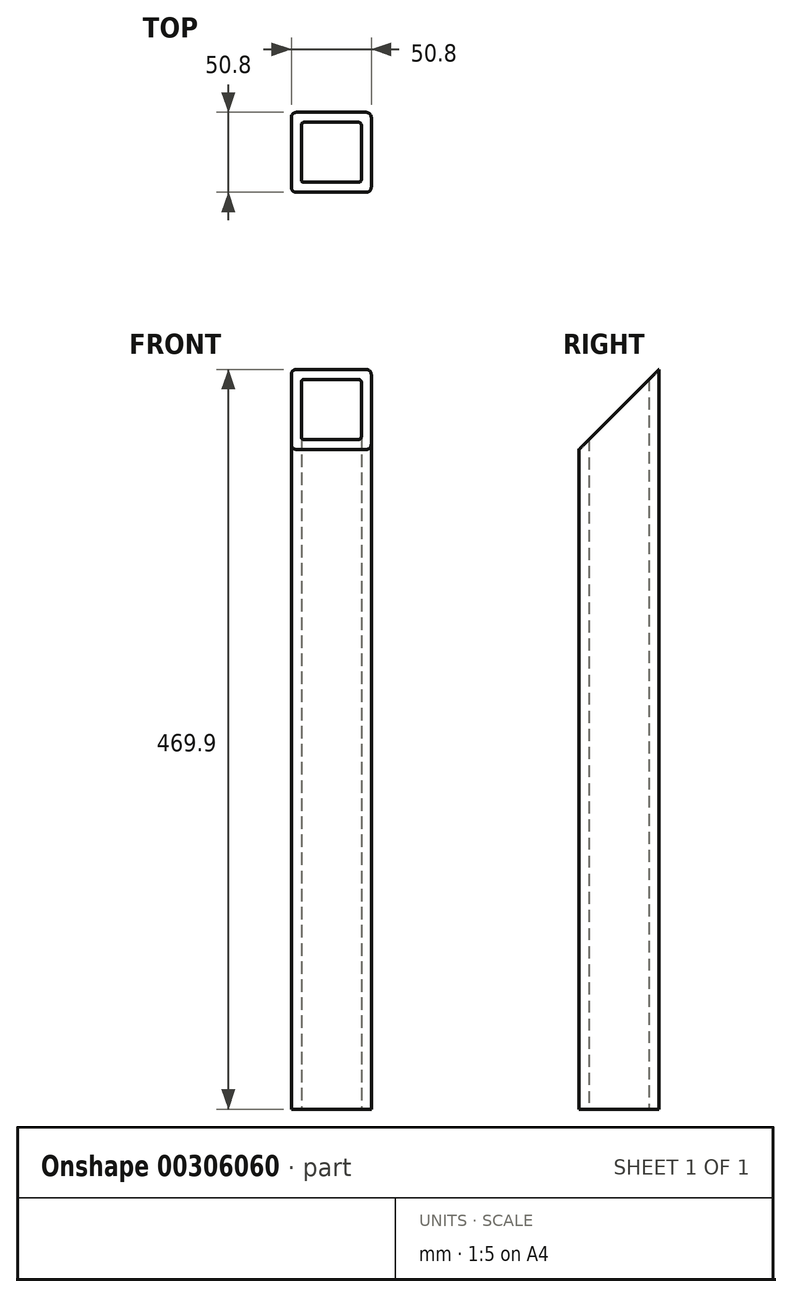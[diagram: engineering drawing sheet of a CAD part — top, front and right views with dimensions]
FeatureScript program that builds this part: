
annotation { "Feature Type Name" : "Feature", "Feature Type Description" : "" }
export const myFeature = defineFeature(function(context is Context, id is Id, definition is map)
    precondition{}
    {
        {
            var Q0;
            Q0=qCreatedBy(makeId("Top.planeOp"),FACE);
            var sketch = newSketch(context, id + "F0", { "sketchPlane" : qUnion([Q0])});
            skLineSegment(sketch, "E0.bottom", {"start": v(-22.22, 25.4) * mm, "end": v(22.23, 25.4) * mm});
            skLineSegment(sketch, "E0.top", {"start": v(-22.23, -25.4) * mm, "end": v(22.23, -25.4) * mm});
            skLineSegment(sketch, "E0.left", {"start": v(-25.4, 22.22) * mm, "end": v(-25.4, -22.23) * mm});
            skLineSegment(sketch, "E0.right", {"start": v(25.4, 22.22) * mm, "end": v(25.4, -22.23) * mm});
            skPoint(sketch, "E0.middle", {"position": v(0, 0) * mm});
            skPoint(sketch, "E1.visualSharp", {"position": v(-25.4, 25.4) * mm});
            skArc(sketch, "E1.filletArc", {"start": v(-22.22, 25.4) * mm, "mid": v(-24.47, 24.47) * mm, "end": v(-25.4, 22.22) * mm});
            skPoint(sketch, "E2.visualSharp", {"position": v(-25.4, -25.4) * mm});
            skArc(sketch, "E2.filletArc", {"start": v(-25.4, -22.23) * mm, "mid": v(-24.47, -24.47) * mm, "end": v(-22.23, -25.4) * mm});
            skPoint(sketch, "E3.visualSharp", {"position": v(25.4, -25.4) * mm});
            skArc(sketch, "E3.filletArc", {"start": v(22.23, -25.4) * mm, "mid": v(24.47, -24.47) * mm, "end": v(25.4, -22.23) * mm});
            skPoint(sketch, "E4.visualSharp", {"position": v(25.4, 25.4) * mm});
            skArc(sketch, "E4.filletArc", {"start": v(25.4, 22.22) * mm, "mid": v(24.47, 24.47) * mm, "end": v(22.23, 25.4) * mm});
            skLineSegment(sketch, "E5.0", {"start": v(-17.46, 19.05) * mm, "end": v(17.46, 19.05) * mm});
            skLineSegment(sketch, "E5.1", {"start": v(-19.05, 17.46) * mm, "end": v(-19.05, -17.46) * mm});
            skLineSegment(sketch, "E5.2", {"start": v(-17.46, -19.05) * mm, "end": v(17.46, -19.05) * mm});
            skLineSegment(sketch, "E5.3", {"start": v(19.05, 17.46) * mm, "end": v(19.05, -17.46) * mm});
            skPoint(sketch, "E6.visualSharp", {"position": v(-19.05, 19.05) * mm});
            skArc(sketch, "E6.filletArc", {"start": v(-17.46, 19.05) * mm, "mid": v(-18.59, 18.59) * mm, "end": v(-19.05, 17.46) * mm});
            skPoint(sketch, "E7.visualSharp", {"position": v(-19.05, -19.05) * mm});
            skArc(sketch, "E7.filletArc", {"start": v(-19.05, -17.46) * mm, "mid": v(-18.59, -18.59) * mm, "end": v(-17.46, -19.05) * mm});
            skPoint(sketch, "E8.visualSharp", {"position": v(19.05, -19.05) * mm});
            skArc(sketch, "E8.filletArc", {"start": v(17.46, -19.05) * mm, "mid": v(18.59, -18.59) * mm, "end": v(19.05, -17.46) * mm});
            skPoint(sketch, "E9.visualSharp", {"position": v(19.05, 19.05) * mm});
            skArc(sketch, "E9.filletArc", {"start": v(19.05, 17.46) * mm, "mid": v(18.59, 18.59) * mm, "end": v(17.46, 19.05) * mm});
            skSolve(sketch);
        }
        {
            var Q0;
            Q0=makeQuery(id+"F0.imprint","IMPRINT",FACE,{"disambiguationData":[TD([[makeQuery(id+"F0.imprint","IMPRINT",EDGE,{"derivedFrom":sQuery(id+"F0.wireOp",EDGE,"E0.bottom")}),-1.0]])]});
            extrude(context, id + "F1", {"entities" : qUnion([Q0]), "depth" : 469.9 * mm});
        }
        {
            var Q0;
            Q0=makeQuery(id+"F1.opExtrude","SWEPT_FACE",FACE,{"disambiguationData":[OSD([sQuery(id+"F0.wireOp",EDGE,"E0.right")])]});
            var sketch = newSketch(context, id + "F2", { "sketchPlane" : qUnion([Q0])});
            skLineSegment(sketch, "E10", {"start": v(25.4, 469.9) * mm, "end": v(-25.4, 419.1) * mm});
            skLineSegment(sketch, "E11", {"start": v(-25.4, 419.1) * mm, "end": v(-25.4, 469.9) * mm});
            skLineSegment(sketch, "E12", {"start": v(-25.4, 469.9) * mm, "end": v(25.4, 469.9) * mm});
            skSolve(sketch);
        }
        {
            var Q0;
            Q0=qSketchRegion(id+"F2",true);
            extrude(context, id + "F3", {"entities" : qUnion([Q0]), "operationType" : NewBodyOperationType.REMOVE, "endBound" : BoundingType.THROUGH_ALL, "oppositeDirection" : true, "depth" : 25.4 * mm});
        }
    });
